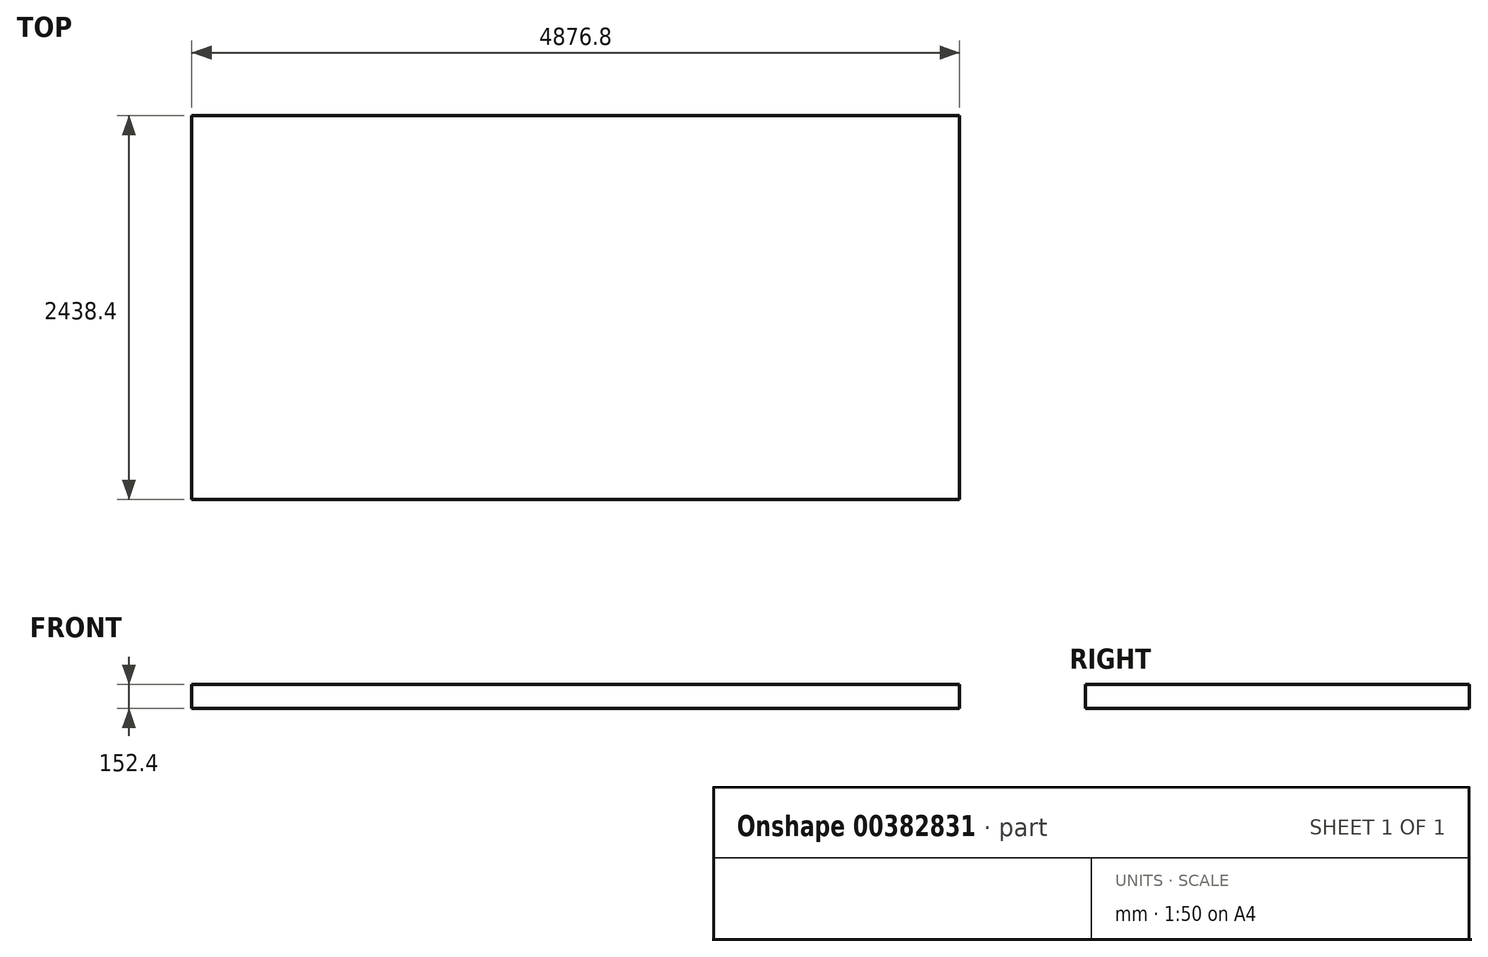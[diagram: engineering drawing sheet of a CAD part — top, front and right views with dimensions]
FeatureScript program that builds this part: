
annotation { "Feature Type Name" : "Feature", "Feature Type Description" : "" }
export const myFeature = defineFeature(function(context is Context, id is Id, definition is map)
    precondition{}
    {
        {
            var Q0;
            Q0=qCreatedBy(makeId("Top.planeOp"),FACE);
            var sketch = newSketch(context, id + "F0", { "sketchPlane" : qUnion([Q0])});
            skLineSegment(sketch, "E0.bottom", {"start": v(-2444.42, 1014.61) * mm, "end": v(2432.38, 1014.61) * mm});
            skLineSegment(sketch, "E0.top", {"start": v(-2444.42, -1423.79) * mm, "end": v(2432.38, -1423.79) * mm});
            skLineSegment(sketch, "E0.left", {"start": v(-2444.42, 1014.61) * mm, "end": v(-2444.42, -1423.79) * mm});
            skLineSegment(sketch, "E0.right", {"start": v(2432.38, 1014.61) * mm, "end": v(2432.38, -1423.79) * mm});
            skSolve(sketch);
        }
        {
            var Q0;
            Q0=makeQuery(id+"F0.imprint","IMPRINT",FACE,{"disambiguationData":[TD([[makeQuery(id+"F0.imprint","IMPRINT",EDGE,{"derivedFrom":sQuery(id+"F0.wireOp",EDGE,"E0.bottom")}),-1.0]])]});
            extrude(context, id + "F1", {"entities" : qUnion([Q0]), "depth" : 152.4 * mm});
        }
    });
